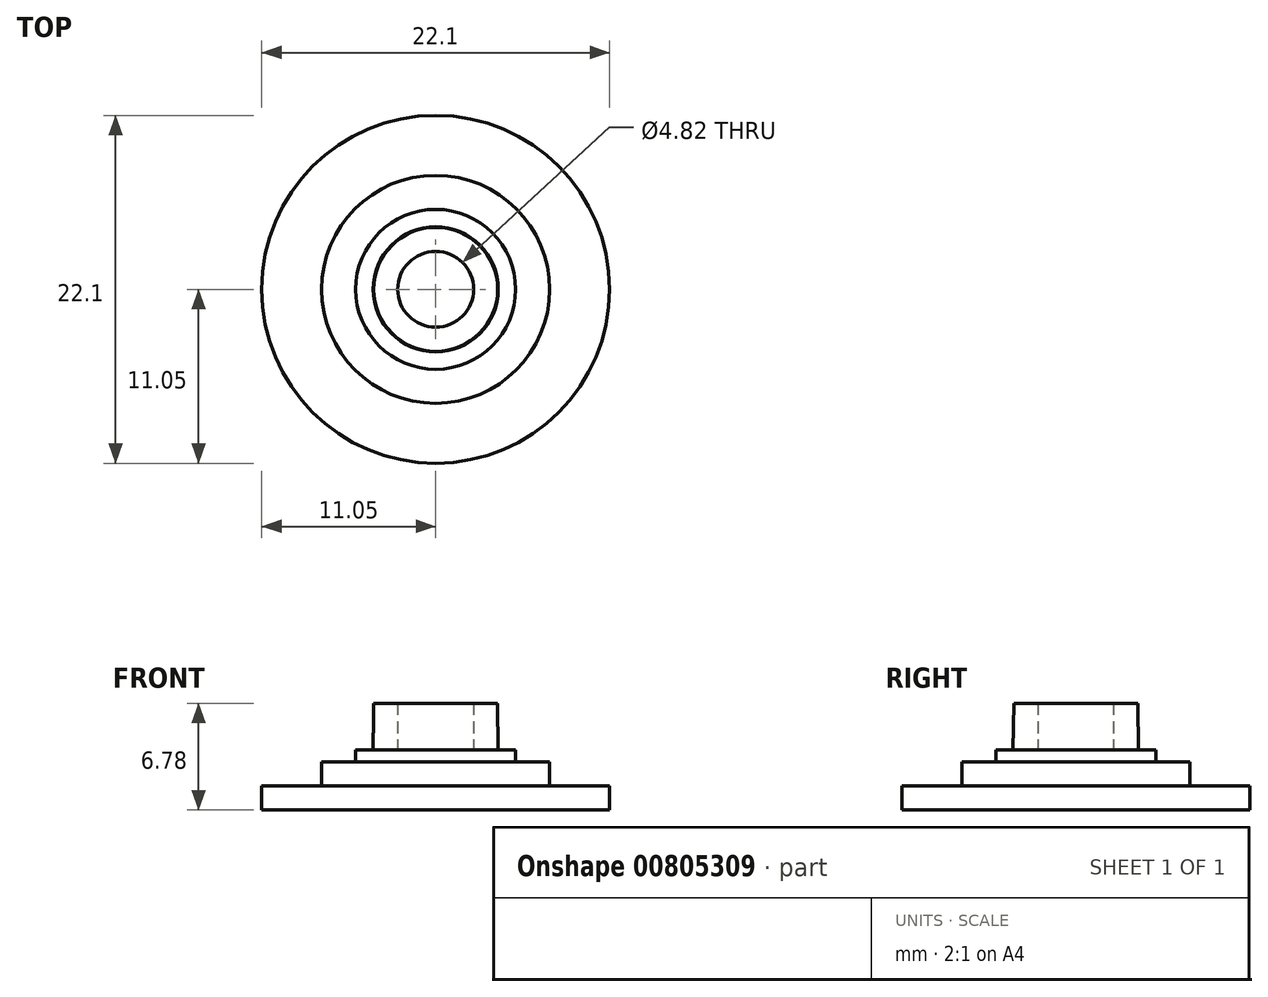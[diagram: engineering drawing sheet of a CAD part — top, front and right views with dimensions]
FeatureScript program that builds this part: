
annotation { "Feature Type Name" : "Feature", "Feature Type Description" : "" }
export const myFeature = defineFeature(function(context is Context, id is Id, definition is map)
    precondition{}
    {
        {
            var Q0;
            Q0=qCreatedBy(makeId("Right.planeOp"),FACE);
            var sketch = newSketch(context, id + "F0", { "sketchPlane" : qUnion([Q0])});
            skLineSegment(sketch, "E0", {"start": v(0, 0) * mm, "end": v(3.98, 0) * mm});
            skLineSegment(sketch, "E1", {"start": v(0, 0) * mm, "end": v(0, 2.97) * mm});
            skLineSegment(sketch, "E2", {"start": v(0, 2.97) * mm, "end": v(3.94, 2.97) * mm});
            skLineSegment(sketch, "E3", {"start": v(3.98, 0) * mm, "end": v(3.94, 2.97) * mm});
            skLineSegment(sketch, "E4", {"start": v(2.4, 2.8) * mm, "end": v(2.4, 2.97) * mm});
            skLineSegment(sketch, "E5", {"start": v(3.98, 0) * mm, "end": v(2.72, -0.17) * mm});
            skLineSegment(sketch, "E6", {"start": v(2.4, 2.8) * mm, "end": v(2.4, 0) * mm});
            skLineSegment(sketch, "E7", {"start": v(2.4, 0) * mm, "end": v(3.98, 0) * mm});
            skSolve(sketch);
        }
        {
            var Q0;
            {var subQ0=sQuery(id+"F0.wireOp",EDGE,"E3");Q0=makeQuery(id+"F0.imprint","IMPRINT",FACE,{"disambiguationData":[TD([[makeQuery(id+"F0.imprint","IMPRINT",EDGE,{"derivedFrom":subQ0}),1.0]])]});}
            var Q1;
            Q1=sQuery(id+"F0.wireOp",EDGE,"E1");
            revolve(context, id + "F1", {"surfaceOperationType" : NewSurfaceOperationType.NEW, "entities" : qUnion([Q0]), "axis" : qUnion([Q1]), "revolveType" : RevolveType.FULL});
        }
        {
            var Q0;
            Q0=qCreatedBy(makeId("Top.planeOp"),FACE);
            var sketch = newSketch(context, id + "F2", { "sketchPlane" : qUnion([Q0])});
            skCircle(sketch, "E8", {"center": v(0, 0) * mm, "radius": 3.94 * mm});
            skCircle(sketch, "E9.0", {"center": v(0, 0) * mm, "radius": 2.67 * mm});
            skSolve(sketch);
        }
        {
            var Q0;
            Q0=qSketchRegion(id+"F2",true);
            extrude(context, id + "F3", {"entities" : qUnion([Q0]), "depth" : 2.8 * mm, "offsetDistance" : 25.4 * mm});
        }
        {
            var Q0;
            Q0=makeQuery(id+"F1.opRevolve","SWEPT_FACE",FACE,{"disambiguationData":[OSD([sQuery(id+"F0.wireOp",EDGE,"E0")])]});
            var sketch = newSketch(context, id + "F4", { "sketchPlane" : qUnion([Q0])});
            skCircle(sketch, "E10", {"center": v(0, 0) * mm, "radius": 5.08 * mm});
            skSolve(sketch);
        }
        {
            var Q0;
            Q0=qSketchRegion(id+"F4",true);
            extrude(context, id + "F5", {"entities" : qUnion([Q0]), "depth" : 0.76 * mm, "offsetDistance" : 25.4 * mm});
        }
        {
            var Q0;
            Q0=makeQuery(id+"F5.opExtrude","CAP_FACE",FACE,{"disambiguationData":[OSD([sQuery(id+"F4.wireOp",EDGE,"E10")])],"isStart":false});
            var sketch = newSketch(context, id + "F6", { "sketchPlane" : qUnion([Q0])});
            skCircle(sketch, "E11", {"center": v(0, 0) * mm, "radius": 7.24 * mm});
            skSolve(sketch);
        }
        {
            var Q0;
            Q0=qSketchRegion(id+"F6",true);
            extrude(context, id + "F7", {"entities" : qUnion([Q0]), "operationType" : NewBodyOperationType.ADD, "depth" : 1.52 * mm, "offsetDistance" : 25.4 * mm});
        }
        {
            var Q0;
            Q0=makeQuery(id+"F3.opExtrude","SWEPT_BODY",BODY,{"disambiguationData":[OSD([sQuery(id+"F2.wireOp",EDGE,"E8"),sQuery(id+"F2.wireOp",EDGE,"E9.0")])]});
            deleteBodies(context, id + "F8", {"entities" : qUnion([Q0])});
        }
        {
            var Q0;
            Q0=makeQuery(id+"F7.opExtrude","CAP_FACE",FACE,{"disambiguationData":[OSD([sQuery(id+"F6.wireOp",EDGE,"E11")])],"isStart":false});
            var sketch = newSketch(context, id + "F9", { "sketchPlane" : qUnion([Q0])});
            skCircle(sketch, "E12", {"center": v(0, 0) * mm, "radius": 11.05 * mm});
            skSolve(sketch);
        }
        {
            var Q0;
            Q0 = qSketchRegion(id + "F9", true);
            extrude(context, id + "F10", {"entities" : qUnion([Q0]), "operationType" : NewBodyOperationType.ADD, "depth" : 1.52 * mm, "offsetDistance" : 25.4 * mm});
        }
    });
